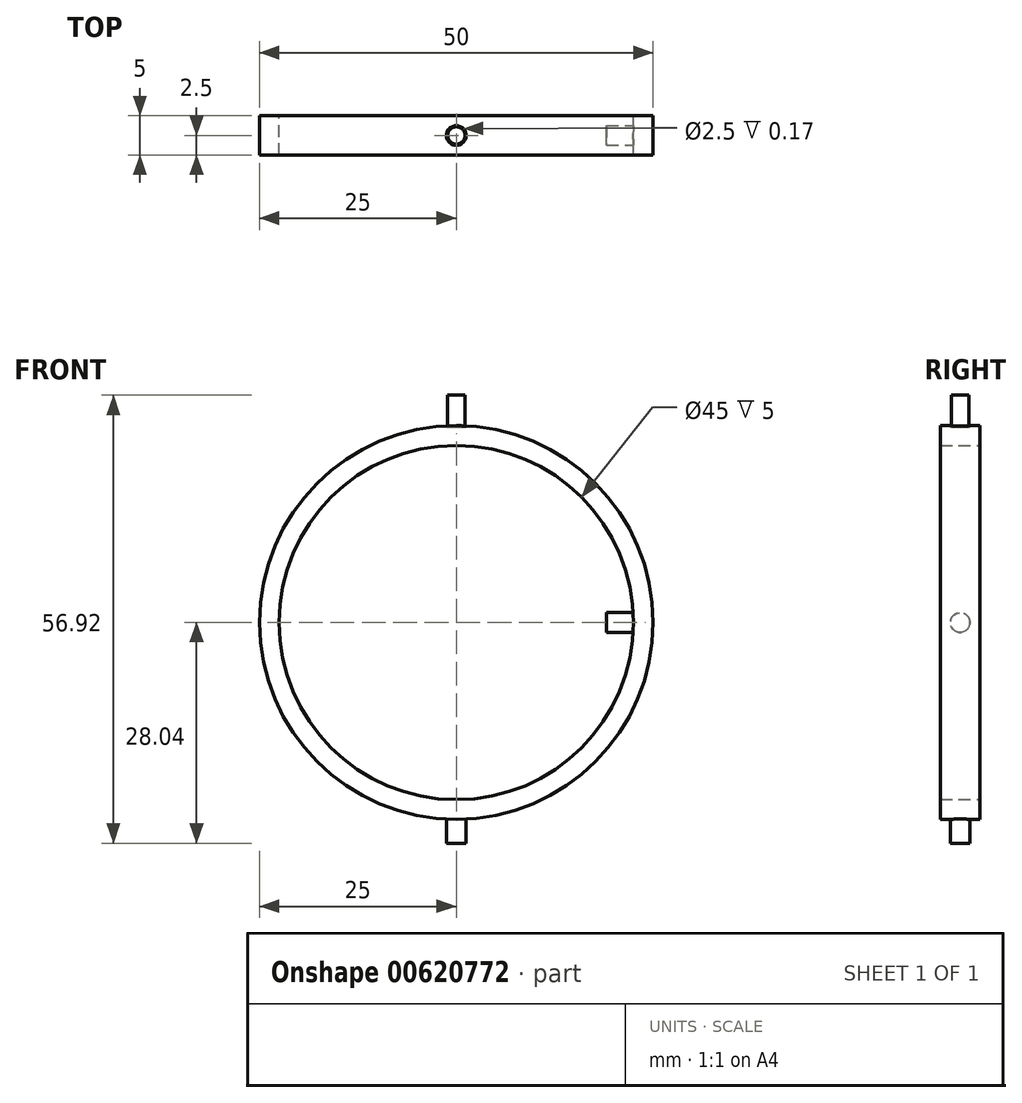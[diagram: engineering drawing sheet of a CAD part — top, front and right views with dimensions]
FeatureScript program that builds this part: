
annotation { "Feature Type Name" : "Feature", "Feature Type Description" : "" }
export const myFeature = defineFeature(function(context is Context, id is Id, definition is map)
    precondition{}
    {
        {
            var Q0;
            Q0=qCreatedBy(makeId("Front.planeOp"),FACE);
            var sketch = newSketch(context, id + "F0", { "sketchPlane" : qUnion([Q0])});
            skCircle(sketch, "E0", {"center": v(0, 0) * mm, "radius": 25 * mm});
            skCircle(sketch, "E1", {"center": v(0, 0) * mm, "radius": 22.5 * mm});
            skSolve(sketch);
        }
        {
            var Q0;
            Q0 = qSketchRegion(id + "F0", true);
            extrude(context, id + "F1", {"entities" : qUnion([Q0]), "depth" : 5 * mm, "offsetDistance" : 25 * mm});
        }
        {
            var Q0;
            Q0=qCreatedBy(makeId("Top.planeOp"),FACE);
            cPlane(context, id + "F2", {"entities" : qUnion([Q0]), "cplaneType" : CPlaneType.OFFSET, "offset" : 24.83 * mm, "width" : 150 * mm, "height" : 150 * mm});
        }
        {
            var Q0;
            Q0=qCreatedBy(id+"F2.planeOp",FACE);
            var sketch = newSketch(context, id + "F3", { "sketchPlane" : qUnion([Q0])});
            skCircle(sketch, "E2", {"center": v(0, -2.5) * mm, "radius": 1.25 * mm});
            skSolve(sketch);
        }
        {
            var Q0;
            Q0 = qSketchRegion(id + "F3", true);
            extrude(context, id + "F4", {"entities" : qUnion([Q0]), "operationType" : NewBodyOperationType.ADD, "depth" : 3.8 * mm, "offsetDistance" : 25 * mm});
        }
        {
            var Q0;
            Q0=qCreatedBy(makeId("Top.planeOp"),FACE);
            cPlane(context, id + "F5", {"entities" : qUnion([Q0]), "cplaneType" : CPlaneType.OFFSET, "offset" : 24.39 * mm, "oppositeDirection" : true, "width" : 150 * mm, "height" : 150 * mm});
        }
        {
            var Q0;
            Q0=qCreatedBy(id+"F5.planeOp",FACE);
            var sketch = newSketch(context, id + "F6", { "sketchPlane" : qUnion([Q0])});
            skCircle(sketch, "E3", {"center": v(0, -2.5) * mm, "radius": 1.25 * mm});
            skSolve(sketch);
        }
        {
            var Q0;
            Q0 = qSketchRegion(id + "F6", true);
            extrude(context, id + "F7", {"entities" : qUnion([Q0]), "operationType" : NewBodyOperationType.ADD, "oppositeDirection" : true, "depth" : 3.4 * mm, "offsetDistance" : 25 * mm});
        }
        {
            var Q0;
            Q0=makeQuery(id+"F7.opExtrude","CAP_FACE",FACE,{"disambiguationData":[OSD([sQuery(id+"F6.wireOp",EDGE,"E3")])],"isStart":false});
            var sketch = newSketch(context, id + "F8", { "sketchPlane" : qUnion([Q0])});
            skCircle(sketch, "E4", {"center": v(0, 2.5) * mm, "radius": 1.25 * mm});
            skSolve(sketch);
        }
        {
            var Q0;
            Q0=makeQuery(id+"F8.imprint","IMPRINT",FACE,{"disambiguationData":[TD([[makeQuery(id+"F8.imprint","IMPRINT",EDGE,{"derivedFrom":sQuery(id+"F8.wireOp",EDGE,"E4")}),-1.0]])]});
            extrude(context, id + "F9", {"entities" : qUnion([Q0]), "operationType" : NewBodyOperationType.ADD, "depth" : .25 * mm, "offsetDistance" : 25 * mm});
        }
        {
            var Q0;
            Q0=makeQuery(id+"F4.opExtrude","CAP_FACE",FACE,{"disambiguationData":[OSD([sQuery(id+"F3.wireOp",EDGE,"E2")])],"isStart":false});
            var sketch = newSketch(context, id + "F10", { "sketchPlane" : qUnion([Q0])});
            skCircle(sketch, "E5", {"center": v(0, -2.5) * mm, "radius": 1.25 * mm});
            skSolve(sketch);
        }
        {
            var Q0;
            Q0 = qSketchRegion(id + "F10", true);
            extrude(context, id + "F11", {"entities" : qUnion([Q0]), "operationType" : NewBodyOperationType.ADD, "depth" : 0.25 * mm, "offsetDistance" : 25 * mm});
        }
        {
            var Q0;
            Q0=qCreatedBy(makeId("Top.planeOp"),FACE);
            cPlane(context, id + "F12", {"entities" : qUnion([Q0]), "cplaneType" : CPlaneType.OFFSET, "offset" : 17.8 * mm, "width" : 150 * mm, "height" : 150 * mm});
        }
        {
            var Q0;
            Q0=qCreatedBy(id+"F2.planeOp",FACE);
            var sketch = newSketch(context, id + "F13", { "sketchPlane" : qUnion([Q0])});
            skCircle(sketch, "E6.0.0", {"center": v(0, -2.5) * mm, "radius": 1.25 * mm});
            skCircle(sketch, "E7", {"center": v(0, -2.5) * mm, "radius": 1.1 * mm});
            skSolve(sketch);
        }
        {
            var Q0;
            Q0 = qSketchRegion(id + "F13", true);
            extrude(context, id + "F14", {"entities" : qUnion([Q0]), "operationType" : NewBodyOperationType.REMOVE, "depth" : 25 * mm, "offsetDistance" : 25 * mm});
        }
        {
            var Q0;
            Q0=qCreatedBy(makeId("Right.planeOp"),FACE);
            cPlane(context, id + "F15", {"entities" : qUnion([Q0]), "cplaneType" : CPlaneType.OFFSET, "offset" : 23.5 * mm, "width" : 150 * mm, "height" : 150 * mm});
        }
        {
            var Q0;
            Q0=qCreatedBy(id+"F15.planeOp",FACE);
            var sketch = newSketch(context, id + "F16", { "sketchPlane" : qUnion([Q0])});
            skCircle(sketch, "E8", {"center": v(-2.5, 0) * mm, "radius": 1.25 * mm});
            skSolve(sketch);
        }
        {
            var Q0;
            Q0 = qSketchRegion(id + "F16", true);
            extrude(context, id + "F17", {"entities" : qUnion([Q0]), "operationType" : NewBodyOperationType.ADD, "oppositeDirection" : true, "depth" : 4.4 * mm, "offsetDistance" : 25 * mm});
        }
    });
